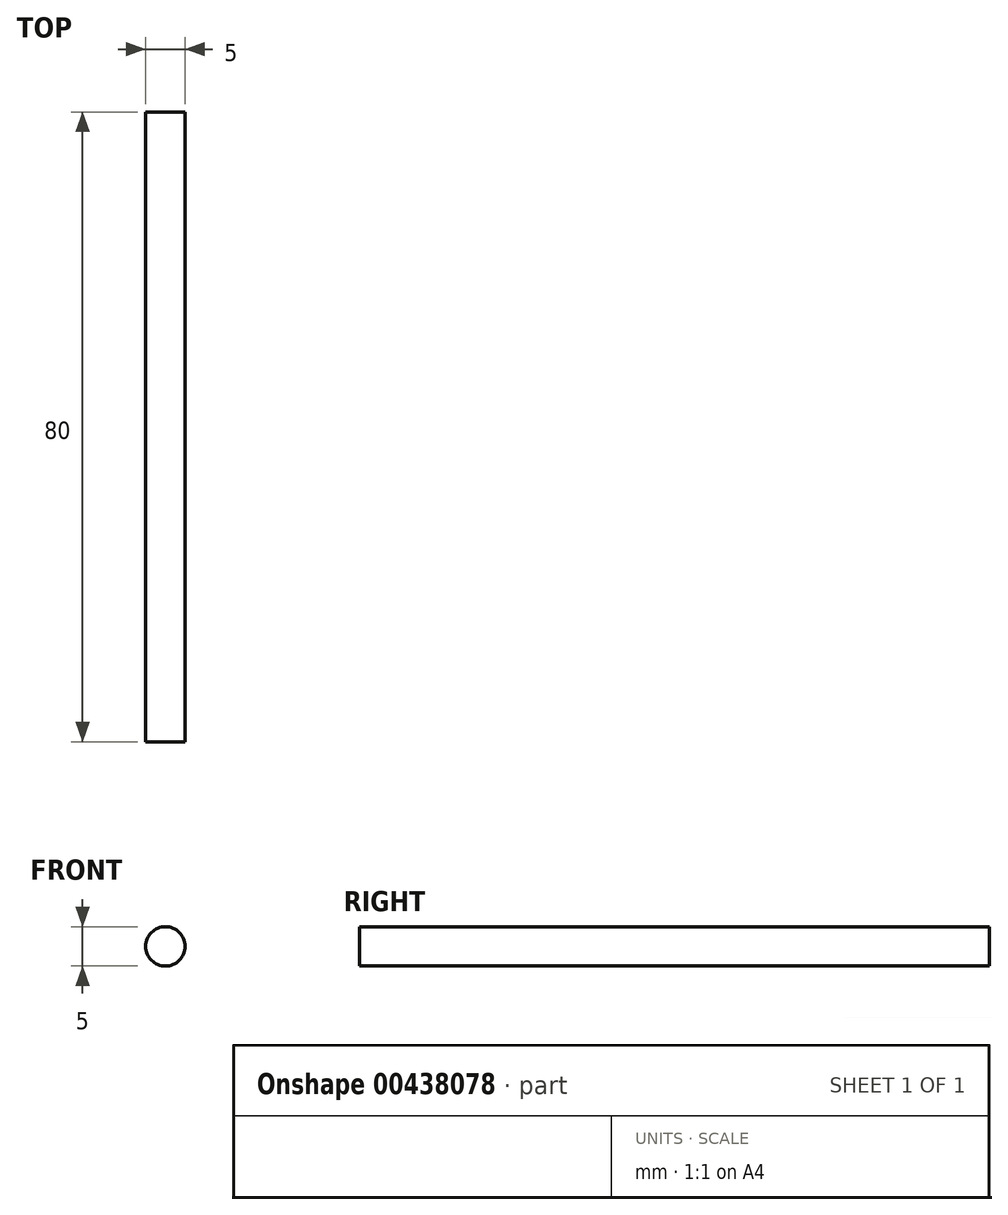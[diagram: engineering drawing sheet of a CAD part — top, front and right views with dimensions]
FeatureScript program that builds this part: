
annotation { "Feature Type Name" : "Feature", "Feature Type Description" : "" }
export const myFeature = defineFeature(function(context is Context, id is Id, definition is map)
    precondition{}
    {
        {
            var Q0;
            Q0=qCreatedBy(makeId("Front.planeOp"),FACE);
            var sketch = newSketch(context, id + "F0", { "sketchPlane" : qUnion([Q0])});
            skCircle(sketch, "E0", {"center": v(0, 0) * mm, "radius": 2.5 * mm});
            skSolve(sketch);
        }
        {
            var Q0;
            Q0=sQuery(id+"F0.wireOp",EDGE,"E0");
            extrude(context, id + "F1", {"bodyType" : ToolBodyType.SURFACE, "surfaceEntities" : qUnion([Q0]), "endBound" : BoundingType.SYMMETRIC, "depth" : 80 * mm});
        }
    });
